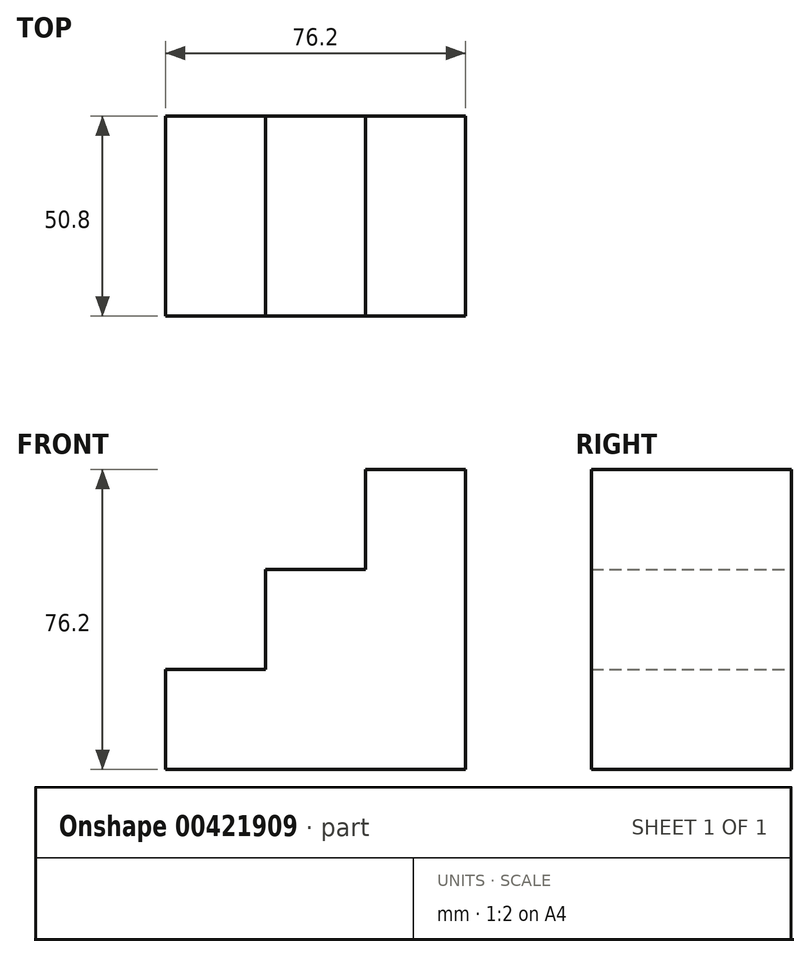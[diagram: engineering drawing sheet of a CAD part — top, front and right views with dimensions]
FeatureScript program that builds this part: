
annotation { "Feature Type Name" : "Feature", "Feature Type Description" : "" }
export const myFeature = defineFeature(function(context is Context, id is Id, definition is map)
    precondition{}
    {
        {
            var Q0;
            Q0=qCreatedBy(makeId("Front.planeOp"),FACE);
            var sketch = newSketch(context, id + "F0", { "sketchPlane" : qUnion([Q0])});
            skLineSegment(sketch, "E0", {"start": v(-52.14, 0) * mm, "end": v(24.06, 0) * mm});
            skLineSegment(sketch, "E1", {"start": v(24.06, 0) * mm, "end": v(24.06, 76.2) * mm});
            skLineSegment(sketch, "E2", {"start": v(-52.14, 0) * mm, "end": v(-52.14, 25.4) * mm});
            skLineSegment(sketch, "E3", {"start": v(-52.14, 25.4) * mm, "end": v(-26.74, 25.4) * mm});
            skLineSegment(sketch, "E4", {"start": v(-26.74, 25.4) * mm, "end": v(-26.74, 50.8) * mm});
            skLineSegment(sketch, "E5", {"start": v(-26.74, 50.8) * mm, "end": v(-1.34, 50.8) * mm});
            skLineSegment(sketch, "E6", {"start": v(-1.34, 50.8) * mm, "end": v(-1.34, 76.2) * mm});
            skLineSegment(sketch, "E7", {"start": v(-1.34, 76.2) * mm, "end": v(24.06, 76.2) * mm});
            skSolve(sketch);
        }
        {
            var Q0;
            Q0=makeQuery(id+"F0.imprint","IMPRINT",FACE,{"disambiguationData":[TD([[makeQuery(id+"F0.imprint","IMPRINT",EDGE,{"derivedFrom":sQuery(id+"F0.wireOp",EDGE,"E0")}),1.0]])]});
            extrude(context, id + "F1", {"entities" : qUnion([Q0]), "depth" : 50.8 * mm});
        }
    });
